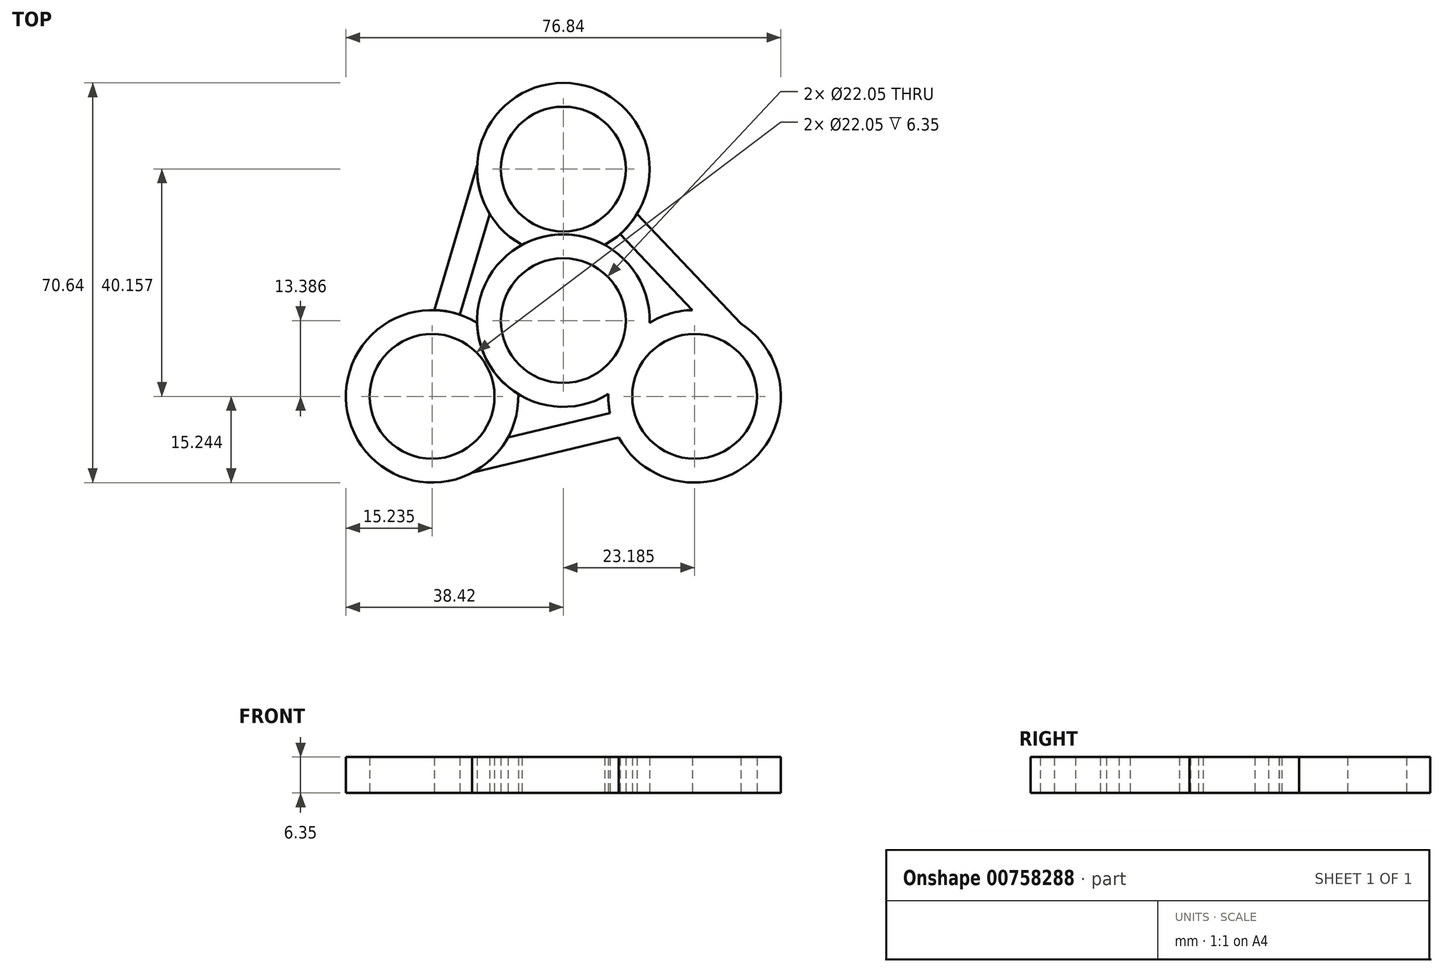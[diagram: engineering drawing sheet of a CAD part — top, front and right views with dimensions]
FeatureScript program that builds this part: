
annotation { "Feature Type Name" : "Feature", "Feature Type Description" : "" }
export const myFeature = defineFeature(function(context is Context, id is Id, definition is map)
    precondition{}
    {
        {
            var Q0;
            Q0=qCreatedBy(makeId("Top.planeOp"),FACE);
            var sketch = newSketch(context, id + "F0", { "sketchPlane" : qUnion([Q0])});
            skCircle(sketch, "E0", {"center": v(0, 0) * mm, "radius": 11.02 * mm});
            skCircle(sketch, "E1", {"center": v(0, 0) * mm, "radius": 15.24 * mm});
            skCircle(sketch, "E2", {"center": v(0, 26.77) * mm, "radius": 15.24 * mm});
            skCircle(sketch, "E3", {"center": v(0, 26.77) * mm, "radius": 11.02 * mm});
            skCircle(sketch, "E4.1.0", {"center": v(-23.18, -13.39) * mm, "radius": 15.24 * mm});
            skCircle(sketch, "E4.1.1", {"center": v(-23.18, -13.39) * mm, "radius": 11.02 * mm});
            skCircle(sketch, "E4.2.0", {"center": v(23.18, -13.39) * mm, "radius": 15.24 * mm});
            skCircle(sketch, "E4.2.1", {"center": v(23.18, -13.39) * mm, "radius": 11.02 * mm});
            skSolve(sketch);
        }
        {
            var Q0;
            Q0=qCreatedBy(makeId("Top.planeOp"),FACE);
            var sketch = newSketch(context, id + "F1", { "sketchPlane" : qUnion([Q0])});
            skCircle(sketch, "E5.0", {"center": v(0, 26.77) * mm, "radius": 15.24 * mm});
            skCircle(sketch, "E6.0", {"center": v(0, 26.77) * mm, "radius": 11.02 * mm});
            skCircle(sketch, "E7.0", {"center": v(0, 0) * mm, "radius": 15.24 * mm});
            skCircle(sketch, "E8.0", {"center": v(0, 0) * mm, "radius": 11.02 * mm});
            skCircle(sketch, "E9.0", {"center": v(-23.18, -13.39) * mm, "radius": 15.24 * mm});
            skCircle(sketch, "E10.0", {"center": v(-23.18, -13.39) * mm, "radius": 11.02 * mm});
            skCircle(sketch, "E11.0", {"center": v(23.18, -13.39) * mm, "radius": 15.24 * mm});
            skLineSegment(sketch, "E12", {"start": v(10.03, 15.3) * mm, "end": v(22.79, 1.85) * mm});
            skLineSegment(sketch, "E13", {"start": v(13, 18.82) * mm, "end": v(31.35, -0.52) * mm});
            skLineSegment(sketch, "E14.1.0", {"start": v(-22.8, 1.85) * mm, "end": v(-15.23, 27.41) * mm});
            skLineSegment(sketch, "E14.1.1", {"start": v(-18.26, 1.04) * mm, "end": v(-13, 18.8) * mm});
            skLineSegment(sketch, "E14.2.0", {"start": v(9.8, -20.67) * mm, "end": v(-16.13, -26.9) * mm});
            skLineSegment(sketch, "E14.2.1", {"start": v(8.23, -16.33) * mm, "end": v(-9.8, -20.66) * mm});
            skCircle(sketch, "E15.0", {"center": v(23.18, -13.39) * mm, "radius": 11.02 * mm});
            skSolve(sketch);
        }
        {
            var Q0;
            {var subQ0=sQuery(id+"F1.wireOp",EDGE,"E12");Q0=makeQuery(id+"F1.imprint","IMPRINT",FACE,{"disambiguationData":[TD([[makeQuery(id+"F1.imprint","IMPRINT",EDGE,{"derivedFrom":subQ0}),1.0]])]});}
            var Q1;
            {var subQ0=sQuery(id+"F1.wireOp",EDGE,"E14.2.0");Q1=makeQuery(id+"F1.imprint","IMPRINT",FACE,{"disambiguationData":[TD([[makeQuery(id+"F1.imprint","IMPRINT",EDGE,{"derivedFrom":subQ0}),-1.0]])]});}
            var Q2;
            {var subQ0=sQuery(id+"F1.wireOp",EDGE,"E14.1.0");Q2=makeQuery(id+"F1.imprint","IMPRINT",FACE,{"disambiguationData":[TD([[makeQuery(id+"F1.imprint","IMPRINT",EDGE,{"derivedFrom":subQ0}),-1.0]])]});}
            var Q3;
            Q3=makeQuery(id+"F0.imprint","IMPRINT",FACE,{"disambiguationData":[TD([[makeQuery(id+"F0.imprint","IMPRINT",EDGE,{"derivedFrom":sQuery(id+"F0.wireOp",EDGE,"E4.1.1")}),-1.0]])]});
            var Q4;
            {var subQ0=sQuery(id+"F1.wireOp",EDGE,"E9.0");var subQ1=sQuery(id+"F1.wireOp",EDGE,"E7.0");var subQ2=makeQuery(id+"F1.imprint","INTERSECT",VERTEX,{"disambiguationData":[OD(0.0)],"derivedFrom":[subQ1,subQ0]});Q4=makeQuery(id+"F1.imprint","IMPRINT",FACE,{"disambiguationData":[TD([[makeQuery(id+"F1.imprint","IMPRINT",EDGE,{"disambiguationData":[TD([[subQ2,-1.0]])],"derivedFrom":subQ1}),1.0]])]});}
            var Q5;
            Q5=makeQuery(id+"F0.imprint","IMPRINT",FACE,{"disambiguationData":[TD([[makeQuery(id+"F0.imprint","IMPRINT",EDGE,{"derivedFrom":sQuery(id+"F0.wireOp",EDGE,"E3")}),-1.0]])]});
            var Q6;
            {var subQ0=sQuery(id+"F1.wireOp",EDGE,"E7.0");var subQ1=sQuery(id+"F1.wireOp",EDGE,"E5.0");var subQ2=makeQuery(id+"F1.imprint","INTERSECT",VERTEX,{"disambiguationData":[OD(0.0)],"derivedFrom":[subQ1,subQ0]});Q6=makeQuery(id+"F1.imprint","IMPRINT",FACE,{"disambiguationData":[TD([[makeQuery(id+"F1.imprint","IMPRINT",EDGE,{"disambiguationData":[TD([[subQ2,-1.0]])],"derivedFrom":subQ1}),1.0]])]});}
            var Q7;
            Q7=makeQuery(id+"F1.imprint","IMPRINT",FACE,{"disambiguationData":[TD([[makeQuery(id+"F1.imprint","IMPRINT",EDGE,{"derivedFrom":sQuery(id+"F1.wireOp",EDGE,"E15.0")}),-1.0]])]});
            var Q8;
            {var subQ0=sQuery(id+"F1.wireOp",EDGE,"E11.0");var subQ1=sQuery(id+"F1.wireOp",EDGE,"E7.0");var subQ2=makeQuery(id+"F1.imprint","INTERSECT",VERTEX,{"disambiguationData":[OD(0.0)],"derivedFrom":[subQ1,subQ0]});Q8=makeQuery(id+"F1.imprint","IMPRINT",FACE,{"disambiguationData":[TD([[makeQuery(id+"F1.imprint","IMPRINT",EDGE,{"disambiguationData":[TD([[subQ2,-1.0]])],"derivedFrom":subQ1}),1.0]])]});}
            var Q9;
            Q9=makeQuery(id+"F1.imprint","IMPRINT",FACE,{"disambiguationData":[TD([[makeQuery(id+"F1.imprint","IMPRINT",EDGE,{"derivedFrom":sQuery(id+"F1.wireOp",EDGE,"E8.0")}),-1.0]])]});
            extrude(context, id + "F2", {"entities" : qUnion([Q0, Q1, Q2, Q3, Q4, Q5, Q6, Q7, Q8, Q9]), "depth" : 6.35 * mm, "offsetDistance" : 25.4 * mm});
        }
    });
